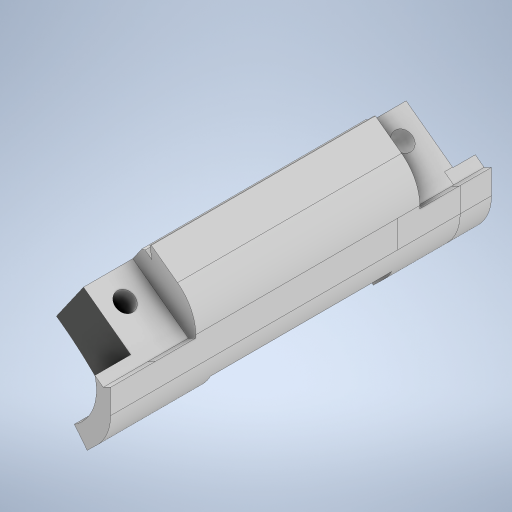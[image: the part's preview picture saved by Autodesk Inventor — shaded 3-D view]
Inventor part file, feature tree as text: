
AUTODESK INVENTOR PART (.ipt)
format: ipt  version: 2023.4 (Build 274418000, 418)  size: 1,946,624 bytes
history: native  units: mm
features: sketch x67, extrude x65, projected_geometry x50, chamfer x19, thicken_offset x7, fillet x4, plane x3, sweep x1
ambient origin geometry x8: Origin, YZ Plane, XZ Plane, XY Plane, X Axis, Y Axis, Z Axis, Center Point
bodies: Solid1 (feature_tree)
feature tree (216):
  extrude  "Extrusion1"  Depth=2.0mm
  extrude  "Extrusion2"  Depth=122.0mm
  extrude  "Extrusion3"  Depth=4.6mm TaperAngle=0.0deg
  extrude  "Extrusion4"  Depth=2.0mm TaperAngle=0.0deg
  extrude  "Extrusion5"  Depth=0.1mm
  thicken_offset  "Thicken1"
  thicken_offset  "Thicken2"
  extrude  "Extrusion6"  Depth=0.1mm
  extrude  "Extrusion7"  Depth=7.0mm TaperAngle=0.0deg
  extrude  "Extrusion8"  Depth=10.0mm TaperAngle=0.0deg
  extrude  "Extrusion9"  Depth=9.0mm TaperAngle=0.0deg
  extrude  "Extrusion10"  Depth=10.0mm TaperAngle=0.0deg
  extrude  "Extrusion11"  Depth=15.0mm TaperAngle=0.0deg
  extrude  "Extrusion12"  Depth=3.0mm
  sketch  "Sketch13"  dims[d40=4.0mm d41=0.0mm d42=12.0mm d43=0.0mm]
  plane  "Work Plane1"
  extrude  "Extrusion13"  Depth=12.0mm TaperAngle=0.0deg
  extrude  "Extrusion14"  Depth=7.0mm TaperAngle=0.0deg
  extrude  "Extrusion15"  Depth=5.0mm TaperAngle=0.0deg
  extrude  "Extrusion16"  Depth=1.0mm TaperAngle=0.0deg
  extrude  "Extrusion17"  Depth=4.0mm TaperAngle=0.0deg
  extrude  "Extrusion18"  Depth=10.0mm TaperAngle=0.0deg
  extrude  "Extrusion19"  Depth=15.0mm TaperAngle=0.0deg
  extrude  "Extrusion20"  Depth=10.0mm TaperAngle=0.0deg
  extrude  "Extrusion21"  Depth=2.0mm TaperAngle=45.0deg
  extrude  "Extrusion22"  Depth=10.0mm TaperAngle=0.0deg
  extrude  "Extrusion23"  Depth=3.0mm TaperAngle=0.0deg
  extrude  "Extrusion24"  Depth=2.0mm TaperAngle=45.0deg
  extrude  "Extrusion25"  Depth=3.0mm TaperAngle=0.0deg
  extrude  "Extrusion28"  Depth=10.0mm
  extrude  "Extrusion29"  Depth=2.0mm TaperAngle=45.0deg
  fillet  "Fillet2"  Radius=4.0mm
  extrude  "Extrusion30"  Depth=4.25mm
  extrude  "Extrusion31"  Depth=4.25mm
  extrude  "Extrusion32"  Depth=9.0mm
  chamfer  "Chamfer4"  Distance=9.0mm
  chamfer  "Chamfer5"  Distance=9.0mm
  chamfer  "Chamfer6"  Distance=6.0mm
  extrude  "Extrusion33"  Depth=6.0mm TaperAngle=0.0deg
  extrude  "Extrusion34"  Depth=9.0mm TaperAngle=0.0deg
  extrude  "Extrusion35"  Depth=30.0mm
  chamfer  "Chamfer7"  Distance=32.5mm
  extrude  "Extrusion36"  Depth=0.2mm
  extrude  "Extrusion37"  Depth=3.0mm TaperAngle=0.0deg
  extrude  "Extrusion38"  Depth=2.0mm TaperAngle=0.0deg
  chamfer  "Chamfer8"  Distance=2.0mm Angle=45.0deg
  chamfer  "Chamfer9"  Distance=2.0mm Angle=45.0deg
  chamfer  "Chamfer10"  Distance=2.0mm Angle=45.0deg
  extrude  "Extrusion39"  Depth=0.2mm
  extrude  "Extrusion40"  Depth=0.2mm
  extrude  "Extrusion41"  Depth=0.2mm
  extrude  "Extrusion42"  Depth=3.0mm TaperAngle=0.0deg
  extrude  "Extrusion43"  Depth=2.0mm TaperAngle=45.0deg
  extrude  "Extrusion44"  Depth=2.0mm
  extrude  "Extrusion45"  Depth=2.5mm
  extrude  "Extrusion46"  Depth=2.0mm TaperAngle=45.0deg
  extrude  "Extrusion47"  Depth=5.0mm TaperAngle=0.0deg
  plane  "Work Plane2"
  extrude  "Extrusion48"  Depth=10.0mm TaperAngle=0.0deg
  extrude  "Extrusion50"  Depth=2.0mm TaperAngle=45.0deg
  thicken_offset  "Thicken3"
  extrude  "Extrusion52"  Depth=3.0mm
  extrude  "Extrusion53"  TaperAngle=0.0deg  [1 undecoded]
  extrude  "Extrusion54"  TaperAngle=0.0deg  [1 undecoded]
  chamfer  "Chamfer13"  [1 undecoded]
  chamfer  "Chamfer14"  Distance=2.0mm Angle=45.0deg
  chamfer  "Chamfer15"  Distance=2.0mm Angle=45.0deg
  fillet  "Fillet3"  [1 undecoded]
  thicken_offset  "Thicken4"
  thicken_offset  "Thicken5"
  thicken_offset  "Thicken6"
  extrude  "Extrusion55"  Depth=40.4mm
  extrude  "Extrusion56"  [1 undecoded]
  extrude  "Extrusion57"  Depth=5.5mm
  chamfer  "Chamfer16"  Distance=1.9mm
  chamfer  "Chamfer18"  Distance=2.0mm
  extrude  "Extrusion58"  Depth=3.0mm
  extrude  "Extrusion59"  [1 undecoded]
  chamfer  "Chamfer19"  [1 undecoded]
  extrude  "Extrusion60"  [1 undecoded]
  extrude  "Extrusion61"  [1 undecoded]
  extrude  "Extrusion62"  [1 undecoded]
  extrude  "Extrusion63"  [1 undecoded]
  chamfer  "Chamfer21"  [1 undecoded]
  chamfer  "Chamfer22"  [1 undecoded]
  fillet  "Fillet4"  [1 undecoded]
  fillet  "Fillet5"  [1 undecoded]
  extrude  "Extrusion64"  [1 undecoded]
  sweep  "Sweep1"
  extrude  "Extrusion65"  [1 undecoded]
  extrude  "Extrusion66"  [1 undecoded]
  thicken_offset  "Thicken7"
  chamfer  "Chamfer23"  [1 undecoded]
  chamfer  "Chamfer24"  [1 undecoded]
  extrude  "Extrusion67"  [1 undecoded]
  plane  "Work Plane3"
  extrude  "Extrusion68"  [1 undecoded]
  extrude  "Extrusion69"  [1 undecoded]
  chamfer  "Chamfer25"  [1 undecoded]
  chamfer  "Chamfer26"  [1 undecoded]
  sketch  "Sketch1"  dims[d0=125.0mm d1=2.0mm]
  sketch  "Sketch2"  dims[d2=4.6mm d3=0.0mm d4=122.0mm]
  sketch  "Sketch3"  dims[d5=42.8mm d6=0.0mm d7=4.6mm d8=0.0mm]
  projected_geometry  "Projected Loop1"
  sketch  "Sketch4"  dims[d10=2.0mm d11=0.0mm d12=2.0mm d13=0.0mm]
  sketch  "Sketch5"  dims[d14=0.1mm d15=0.1mm]
  projected_geometry  "Projected Loop2"
  projected_geometry  "Projected Loop3"
  sketch  "Sketch6"  dims[d16=0.1mm d17=0.1mm]
  projected_geometry  "Projected Loop4"
  sketch  "Sketch7"  dims[d18=0.0mm d19=0.0mm d20=7.0mm d21=0.0mm]
  projected_geometry  "Projected Loop5"
  sketch  "Sketch8"  dims[d22=0.0mm d23=0.0mm d24=10.0mm d25=0.0mm]
  projected_geometry  "Projected Loop6"
  projected_geometry  "Projected Loop7"
  sketch  "Sketch9"  dims[d26=9.0mm d27=0.0mm d28=9.0mm d29=0.0mm]
  projected_geometry  "Projected Loop8"
  sketch  "Sketch10"  dims[d30=10.0mm d31=0.0mm d32=10.0mm d33=0.0mm]
  sketch  "Sketch11"  dims[d34=15.0mm d35=0.0mm d36=15.0mm d37=0.0mm]
  projected_geometry  "Projected Loop9"
  sketch  "Sketch12"  dims[d38=3.0mm d39=3.0mm]
  projected_geometry  "Projected Loop10"
  sketch  "Sketch14"  dims[d44=3.0mm d45=0.0mm d46=7.0mm d47=0.0mm]
  projected_geometry  "Projected Loop11"
  projected_geometry  "Projected Loop12"
  sketch  "Sketch15"  dims[d48=2.0mm d49=0.0mm d50=5.0mm d51=0.0mm]
  sketch  "Sketch16"  dims[d52=5.0mm d53=0.0mm d54=1.0mm d55=0.0mm]
  projected_geometry  "Projected Loop13"
  sketch  "Sketch17"  dims[d56=4.0mm d57=0.0mm d58=4.0mm d59=0.0mm]
  sketch  "Sketch18"  dims[d74=10.0mm d75=0.0mm d76=3.9mm d77=0.0mm]
  projected_geometry  "Projected Loop14"
  sketch  "Sketch19"  dims[d78=3.0mm d79=15.0mm d80=0.0mm]
  sketch  "Sketch20"  dims[d81=15.0mm d82=0.0mm d83=10.0mm d84=0.0mm]
  projected_geometry  "Projected Loop15"
  sketch  "Sketch21"  dims[d85=4.0mm d86=2.0mm d87=45.0deg d88=1.3mm d89=2.0mm d90=45.0deg]
  projected_geometry  "Projected Loop16"
  sketch  "Sketch22"  dims[d91=3.0mm d92=2.0mm d93=45.0deg d94=10.0mm d95=0.0mm]
  projected_geometry  "Projected Loop17"
  projected_geometry  "Projected Loop18"
  projected_geometry  "Projected Loop19"
  projected_geometry  "Projected Loop20"
  projected_geometry  "Projected Loop21"
  projected_geometry  "Projected Loop22"
  projected_geometry  "Projected Loop23"
  projected_geometry  "Projected Loop24"
  projected_geometry  "Projected Loop25"
  projected_geometry  "Projected Loop26"
  sketch  "Sketch24"  dims[d96=2.0mm d97=3.0mm d98=0.0mm]
  projected_geometry  "Projected Loop28"
  sketch  "Sketch25"  dims[d99=3.0mm d100=0.0mm d101=2.0mm d102=2.0mm d103=45.0deg]
  sketch  "Sketch26"  dims[d104=6.0mm d105=3.0mm d106=0.0mm]
  sketch  "Sketch29"  dims[d107=10.0mm d108=0.0mm d109=11.2mm]
  projected_geometry  "Projected Loop31"
  sketch  "Sketch30"  dims[d110=6.0mm d111=0.0mm d112=4.0mm d113=2.0mm d114=45.0deg]
  projected_geometry  "Projected Loop32"
  sketch  "Sketch31"  dims[d115=2.0mm d116=2.0mm d117=45.0deg]
  sketch  "Sketch32"  dims[d118=1.0mm d119=2.0mm d120=45.0deg d121=4.0mm d122=0.0mm]
  sketch  "Sketch33"  dims[d123=4.25mm d124=4.25mm]
  sketch  "Sketch34"  dims[d125=4.25mm d126=4.25mm]
  sketch  "Sketch35"  dims[d127=9.0mm d128=0.0mm d129=4.25mm]
  sketch  "Sketch36"  dims[d130=4.25mm d131=9.0mm d132=0.0mm]
  projected_geometry  "Projected Loop33"
  sketch  "Sketch37"  dims[d133=4.25mm]
  projected_geometry  "Projected Loop34"
  sketch  "Sketch38"  dims[d134=4.25mm d135=9.0mm d136=0.0mm d137=6.0mm d138=0.0mm]
  projected_geometry  "Projected Loop35"
  sketch  "Sketch39"  dims[d139=6.0mm d140=0.0mm d141=6.0mm d142=0.0mm]
  sketch  "Sketch40"  dims[d143=9.0mm d144=0.0mm d145=4.0mm d146=0.0mm]
  projected_geometry  "Projected Loop36"
  sketch  "Sketch41"  dims[d147=-5.0mm d148=30.0mm d149=32.5mm d150=0.0mm]
  sketch  "Sketch42"  dims[d153=10.0mm d154=0.0mm d163=0.2mm]
  sketch  "Sketch43"  dims[d164=0.2mm d165=3.0mm d166=0.0mm]
  sketch  "Sketch44"  dims[d167=2.0mm d168=0.0mm d169=2.0mm d170=0.0mm d171=4.0mm d172=2.0mm d173=45.0deg d174=4.0mm d175=2.0mm d176=45.0deg d177=0.5mm d178=2.0mm d179=45.0deg]
  sketch  "Sketch45"  dims[d180=10.0mm d181=0.2mm]
  projected_geometry  "Projected Loop37"
  sketch  "Sketch46"  dims[d182=0.2mm d183=0.2mm d184=0.2mm]
  projected_geometry  "Projected Loop38"
  sketch  "Sketch47"  dims[d185=0.2mm d186=0.2mm]
  projected_geometry  "Projected Loop39"
  sketch  "Sketch48"  dims[d187=3.0mm d188=0.0mm d189=3.0mm d190=0.0mm]
  projected_geometry  "Projected Loop40"
  sketch  "Sketch49"  dims[d191=5.0mm d192=0.0mm d193=4.0mm d194=2.0mm d195=45.0deg]
  sketch  "Sketch51"  dims[d199=4.0mm d200=2.0mm d201=45.0deg d202=4.5mm]
  projected_geometry  "Projected Loop41"
  sketch  "Sketch53"  dims[d203=0.0mm d204=0.0mm d205=2.5mm]
  projected_geometry  "Projected Loop42"
  sketch  "Sketch54"  dims[d206=10.0mm d207=0.0mm d208=4.0mm d209=2.0mm d210=45.0deg]
  projected_geometry  "Projected Loop43"
  projected_geometry  "Projected Loop44"
  sketch  "Sketch55"  dims[d211=10.0mm d212=0.0mm d216=5.0mm d217=0.0mm]
  projected_geometry  "Projected Loop45"
  projected_geometry  "Projected Loop46"
  sketch  "Sketch56"  dims[d218=5.0mm d219=0.0mm d220=10.0mm d221=0.0mm]
  projected_geometry  "Projected Loop47"
  sketch  "Sketch57"  dims[d222=4.0mm d223=2.0mm d224=45.0deg d225=4.0mm d226=2.0mm d227=45.0deg]
  projected_geometry  "Projected Loop48"
  sketch  "Sketch58"  dims[d228=3.0mm d229=3.0mm]
  projected_geometry  "Projected Loop49"
  sketch  "Sketch59"  dims[d230=6.108652mm d231=0.0mm d232=0.0mm]
  sketch  "Sketch60"  dims[d233=0.0mm d234=0.0mm d235=0.0mm d236=0.0mm d237=0.0mm d238=0.0mm]
  sketch  "Sketch61"  dims[d239=0.15mm]
  sketch  "Sketch62"  dims[d240=0.15mm d241=0.5mm d242=2.0mm d243=45.0deg d244=0.5mm d245=2.0mm d246=45.0deg d247=0.0mm]
  projected_geometry  "Projected Loop50"
  sketch  "Sketch63"  dims[d248=6.15mm d249=40.4mm]
  sketch  "Sketch64"  dims[d250=0.0mm d251=0.0mm d252=-6.9mm]
  projected_geometry  "Projected Loop51"
  projected_geometry  "Projected Loop52"
  sketch  "Sketch65"  dims[d253=5.5mm d254=5.5mm]
  sketch  "Sketch66"  dims[d255=3.0mm d256=1.9mm d257=0.0mm d258=2.0mm d259=0.0mm]
  projected_geometry  "Projected Loop53"
  sketch  "3D Sketch1"
  sketch  "Sketch67"  dims[d260=1.0mm d261=2.0mm d262=12.217305mm d263=3.0mm d264=2.0mm d265=12.217305mm]
  sketch  "Sketch68"  dims[d9=0.5mm]
  sketch  "Sketch69"
  sketch  "Sketch70"
  sketch  "Sketch71"
note: 25 required parameter values undecoded (feature->parameter linkage not recoverable at this tier; creation-order binding heuristic only, values carry confidence <= 0.55)
